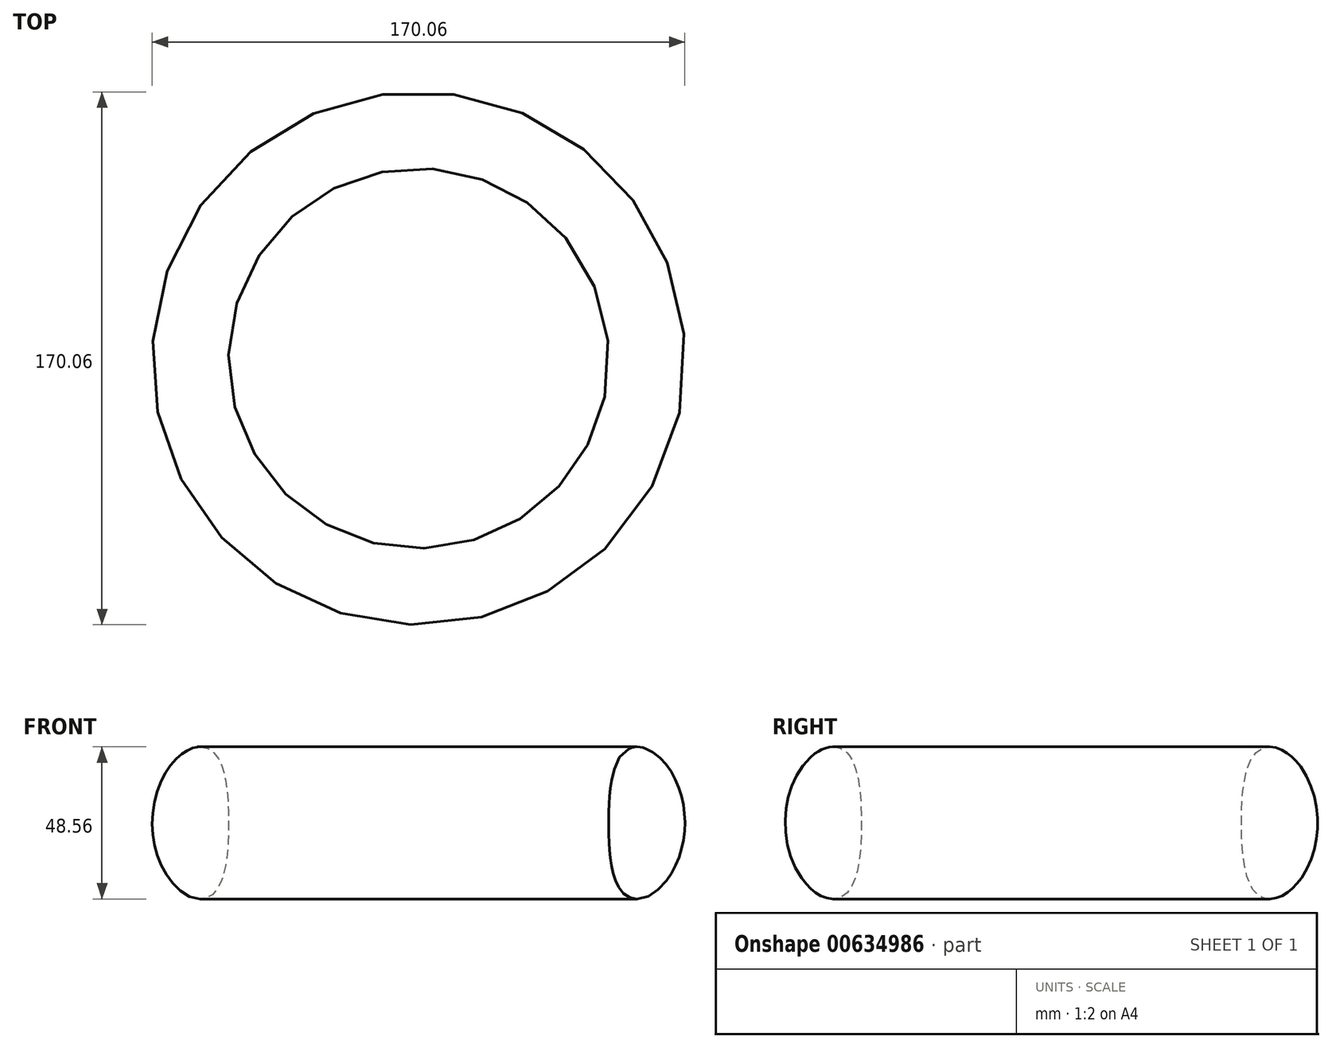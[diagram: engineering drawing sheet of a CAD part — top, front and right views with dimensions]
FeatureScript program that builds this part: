
annotation { "Feature Type Name" : "Feature", "Feature Type Description" : "" }
export const myFeature = defineFeature(function(context is Context, id is Id, definition is map)
    precondition{}
    {
        {
            var Q0;
            Q0=qCreatedBy(makeId("Front.planeOp"),FACE);
            var sketch = newSketch(context, id + "F0", { "sketchPlane" : qUnion([Q0])});
            skLineSegment(sketch, "E0.bottom", {"start": v(63.98, 0) * mm, "end": v(-59.4, 0) * mm});
            skLineSegment(sketch, "E0.top", {"start": v(63.98, 67.34) * mm, "end": v(-59.4, 67.34) * mm});
            skLineSegment(sketch, "E0.left", {"start": v(63.98, 0) * mm, "end": v(63.98, 67.34) * mm});
            skLineSegment(sketch, "E0.right", {"start": v(-59.4, 0) * mm, "end": v(-59.4, 67.34) * mm});
            skSolve(sketch);
        }
        {
            var Q0;
            Q0=qCreatedBy(makeId("Right.planeOp"),FACE);
            var sketch = newSketch(context, id + "F1", { "sketchPlane" : qUnion([Q0])});
            skCircle(sketch, "E1", {"center": v(-36.56, 0) * mm, "radius": 24.28 * mm});
            skSolve(sketch);
        }
        {
            var Q0;
            Q0 = qSketchRegion(id + "F1", true);
            var Q1;
            Q1=sQuery(id+"F0.wireOp",EDGE,"E0.right");
            revolve(context, id + "F2", {"entities" : qUnion([Q0]), "axis" : qUnion([Q1]), "revolveType" : RevolveType.FULL});
        }
    });
